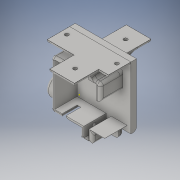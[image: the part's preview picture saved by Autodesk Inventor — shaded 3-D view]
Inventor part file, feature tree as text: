
AUTODESK INVENTOR PART (.ipt)
format: ipt  version: 2016 (Build 200138000, 138)  size: 679,424 bytes
history: native  units: in
note: dims shown in document units (in); Inventor stores cm internally (conversion verified against a paired STEP export)
features: sketch x17, extrude x13, fillet x11, plane x5, hole x3
ambient origin geometry x8: Origin, YZ Plane, XZ Plane, XY Plane, X Axis, Y Axis, Z Axis, Center Point
bodies: Solid1 (feature_tree)
feature tree (49):
  extrude  "Extrusion1"  Depth=0.8976in
  sketch  "Sketch12"  dims[d11=0.0787in d12=0.0787in d13=0.0787in d14=0.0787in d82=0.9016in d83=0.8858in]
  plane  "Work Plane6"
  extrude  "Extrusion5"  Depth=0.9016in
  plane  "Work Plane5"
  hole  "Hole3"  [1 undecoded]
  plane  "Work Plane1"
  extrude  "Extrusion6"  Depth=0.6142in
  extrude  "Extrusion7"  Depth=0.1654in
  plane  "Work Plane4"
  extrude  "Extrusion8"  Depth=0.2165in
  fillet  "Fillet15"  Radius=0.2165in
  plane  "Work Plane3"
  extrude  "Extrusion10"  Depth=0.0787in
  extrude  "Extrusion12"  Depth=0.0787in
  extrude  "Extrusion13"  Depth=0.0787in
  hole  "Hole4"  [1 undecoded]
  extrude  "Extrusion14"  Depth=0.0394in
  extrude  "Extrusion15"  Depth=0.0394in
  fillet  "Fillet19"  Radius=0.1575in
  fillet  "Fillet20"  Radius=0.0787in
  fillet  "Fillet22"  Radius=0.0787in
  fillet  "Fillet23"  Radius=0.0394in
  fillet  "Fillet24"  Radius=0.9016in
  fillet  "Fillet26"  Radius=0.1378in
  sketch  "Sketch37"  dims[d133=0.2165in d136=0.0787in]
  fillet  "Fillet29"  Radius=0.185in
  fillet  "Fillet30"  Radius=0.3543in
  extrude  "Extrusion16"  Depth=0.0787in
  extrude  "Extrusion17"  Depth=0.0394in
  fillet  "Fillet31"  Radius=0.0394in
  fillet  "Fillet32"  Radius=0.7461in
  hole  "Hole5"  [1 undecoded]
  extrude  "Extrusion18"  Depth=0.2835in
  sketch  "Sketch1"  dims[d2=0.1181in d3=0.0in d6=0.8976in d9=0.357in d10=0.7139in]
  sketch  "Sketch14"  dims[d85=0.1063in d86=0.1063in]
  sketch  "Sketch17"  dims[d87=0.6142in d88=0.6142in]
  sketch  "Sketch18"  dims[d89=0.1654in d90=0.1654in]
  sketch  "Sketch22"  dims[d91=0.2992in d92=0.2165in d93=0.2165in]
  sketch  "Sketch24"  dims[d95=0.9016in d97=0.0787in]
  sketch  "Sketch30"  dims[d98=0.0787in d100=0.0787in]
  sketch  "Sketch32"  dims[d101=0.0787in d102=0.0787in]
  sketch  "Sketch33"  dims[d103=0.1693in d105=0.0787in]
  sketch  "Sketch35"  dims[d106=0.0394in d107=0.0394in]
  sketch  "Sketch36"  dims[d108=0.0394in d109=0.0394in d110=0.1575in d111=0.0787in d112=0.0787in d113=0.0394in d114=0.9016in d125=0.1378in d130=0.185in d132=0.3543in]
  sketch  "Sketch38"  dims[d137=0.315in d138=0.0in d139=0.0394in d144=0.0394in d145=0.7461in]
  sketch  "Sketch39"  dims[d146=0.0394in]
  sketch  "Sketch40"  dims[d147=0.07in d148=0.2362in d149=0.119in d150=0.0787in d151=0.5635in d152=0.315in d153=0.8108in d156=0.2717in]
  sketch  "Sketch41"  dims[d157=0.2323in d158=0.2835in d159=0.4016in d160=0.1575in d161=0.0in d164=0.3937in d165=0.0in d166=0.0787in d167=0.0in d171=0.0669in d177=0.0906in d178=0.0in d181=0.0787in d182=0.0787in d185=0.1772in d186=0.0483in d187=0.1063in d188=0.4724in d189=0.0in d190=0.3135in d191=0.4724in d192=0.0in d194=0.2559in d195=0.0394in d196=0.2559in d197=0.0394in d198=0.0787in d199=0.2362in d200=0.1575in d201=0.0787in d202=90.0deg d203=0.315in d204=0.8108in d205=0.1575in d206=0.0in d207=0.0394in d208=0.3937in d209=0.0in d210=0.0787in d211=0.0787in d213=0.0787in d214=0.0591in d215=0.0591in d217=0.0157in d220=0.0591in d221=0.0591in d222=0.5197in d223=0.128in d224=0.128in d225=0.5118in d226=0.0in d227=0.2096in d228=0.5197in d229=0.5118in d230=0.0in d231=0.2362in d232=0.0748in d233=0.2756in d234=0.2598in d235=0.2598in d236=0.2953in d237=0.1181in d238=0.2953in d239=0.1181in d240=0.2953in d241=0.2953in d242=0.2756in d243=0.2598in d244=0.2598in d245=0.0787in d246=0.2362in d247=0.1575in d248=0.0787in d249=90.0deg d250=0.1181in d251=0.8108in d252=0.0394in d253=0.0in d26=0.0394in d27=0.0394in]
note: 3 required parameter values undecoded (feature->parameter linkage not recoverable at this tier; creation-order binding heuristic only, values carry confidence <= 0.55)
